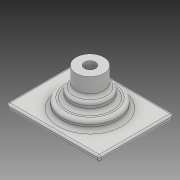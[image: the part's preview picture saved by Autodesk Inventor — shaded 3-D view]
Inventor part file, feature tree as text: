
AUTODESK INVENTOR PART (.ipt)
format: ipt  version: 2018 (Build 220112000, 112)  size: 190,976 bytes
history: native  units: mm
features: extrude x5, sketch x5, fillet x2, other x1
ambient origin geometry x8: Origin, YZ Plane, XZ Plane, XY Plane, X Axis, Y Axis, Z Axis, Center Point
bodies: Body1 (feature_tree)
feature tree (13):
  other  "Sólido1"
  extrude  "Extrusión1"  Depth=50.0mm
  extrude  "Extrusión2"  Depth=3.0mm
  extrude  "Extrusión3"  Depth=5.0mm
  extrude  "Extrusión4"  Depth=15.0mm TaperAngle=0.0deg
  fillet  "Empalme1"  Radius=20.0mm
  fillet  "Empalme2"  Radius=5.0mm
  extrude  "Extrusión5"  Depth=1.0mm
  sketch  "Boceto1"  dims[d0=40.0mm d1=50.0mm]
  sketch  "Boceto2"  dims[d2=3.0mm d3=0.0mm d4=30.0mm]
  sketch  "Boceto3"  dims[d5=5.0mm d6=0.0mm d8=6.0mm]
  sketch  "Boceto4"  dims[d9=15.0mm d10=15.0mm d11=0.0mm d12=20.0mm d13=5.0mm d14=0.0mm]
  sketch  "Boceto5"  dims[d15=2.0mm d16=1.0mm d17=20.0mm d18=0.0mm]
